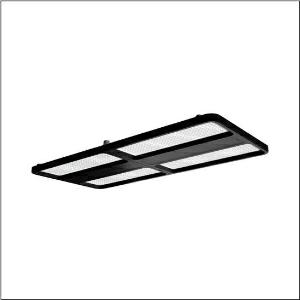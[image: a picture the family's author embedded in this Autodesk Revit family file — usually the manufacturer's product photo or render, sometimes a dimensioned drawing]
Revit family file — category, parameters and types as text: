
# Revit family: highbay_21_maxi_52hn32db4mda
name_source: partatom
category: Lighting Fixtures
units: mm (PartAtom-declared; Revit-internal decimal feet)

## family parameters
Cut with Voids When Loaded = No
Host = Face
Light Source = No
Part Type = Normal
Room Calculation Point = No
Round Connector Dimension = Use Diameter
Shared = No

## types (1)
- --- (1 x LED, 4230 lm, 22.6 W, 4000K)
    Apparent Load = 23 VA
    CIE Flux Codes = 90 98 100 100 100
    Color Rendering = 80
    Color Temperature = 4000K
    Default Elevation = 1800 mm
    Description = high bay luminaire Highbay 21 maxi; direct symmetric wide distribution, light control with lens of PMMA; UGR ≤ 22 (X = 4H | Y = 8H | S = 0.25H | reflection values 70/50/20); luminous flux: 28.000lm; light colour: 840, colour temperature: 4000K, MacAdam ≤ 3 SDCM (initial), colour rendering: CRI > 80; luminous efficacy: 194,4lm/W; rated service life: 75.000h (L80) at AT= ta max; control: DALI 2; luminaire connection: terminal, 5-pole, max. 2.5mm² (cable entry for one cable, Ø 8.5..16mm); mains connection: 230..240V, AC/DC 0/50..60Hz; connected load: 144W; protection rating (complete): IP66; insulation class (complete): insulation class I (protective earthing); protection symbol: D; impact resistance: IK08; certification: CE, ENEC, VDE, UKCA; luminaire for central battery installations according to EN 60598-2-22, internal wiring halogen-free; luminaire LABS conformity tested according to VDMA 24364:2018-05; Suitable for use in the food industry according to the specifications of IFS-Food, HACCP and/or BRC; housing frame of high-performance plastic PA6, matt jet black (RAL 9005); cover of PMMA; dimension (LxWxH): 946 x 442 x 72mm; permissible operating ambient temperature: -40..+65°C (reducing of maximum allowable ambient temperature of 5°C with ceiling mounting); packaging unit: 1 piece; (delivery without accessories; please order mounting accessories separately)
    Height = 72 mm  [stored 0.23622 ft]
    Lamp = 1 x LED
    Lamp Light Flux = 4230 lm
    Lamp Power = 22.6 W
    Lamp count = 1
    Length = 946 mm
    Luminous efficacy = 187 lm/W
    Manufacturer = Siteco
    ModVariant = No
    Model = 52HN32DB4MDA
    Mounting Place = Ceiling
    Mounting Type = Pendant
    Number of Poles = 1
    OnlyDefault = Yes
    Power Factor = 1
    Product Name = Highbay 21 maxi
    Product group = high bay luminaire
    ProductGroupID = 902
    Protection Class = Protection class I
    Protection Degree = IP 66
    RLX_Detail_Level = 1
    RLX_Emergency_Light_Flux = 0 lm
    RLX_Emergency_Type = 0
    RLX_Emergency_Type_DB = No
    RlxData = <blob elided: 133881 chars, md5=9fa1f338>
    Socket = socket
    Standby Power = 0 W
    System Light Flux = 4230 lm
    System Power = 23 W
    Type Comments = : DC mode (central or group accumulator) initial emergency light level
    Type Image = l_1378821.jpg
    URL = http://relux.com
    VarID = @adj_019281
    Voltage = 0 V
    Weight = 0.00 kg
    Width = 442 mm

note: [stored X ft] marks values corroborated as IEEE doubles in the binary element streams (Revit-internal decimal feet)

## geometry (parser evidence)
native form markers: Blend x4, Sweep x11
no freeform markers — native parametric forms only
